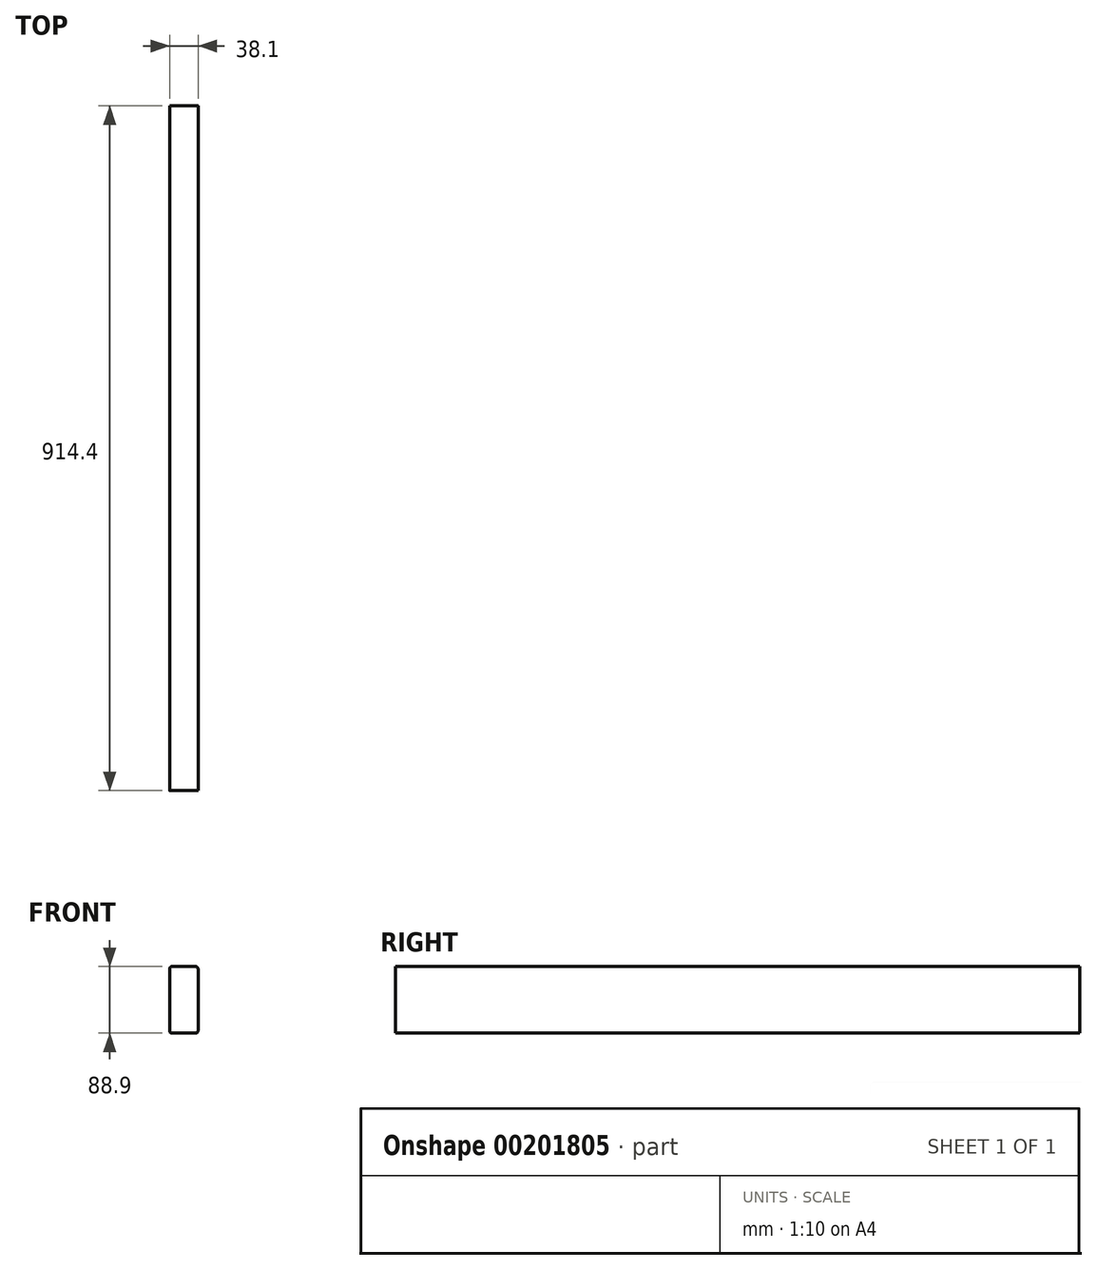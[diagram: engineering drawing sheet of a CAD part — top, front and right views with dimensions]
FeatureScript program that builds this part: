
annotation { "Feature Type Name" : "Feature", "Feature Type Description" : "" }
export const myFeature = defineFeature(function(context is Context, id is Id, definition is map)
    precondition{}
    {
        {
            var Q0;
            Q0=qCreatedBy(makeId("Front.planeOp"),FACE);
            var sketch = newSketch(context, id + "F0", { "sketchPlane" : qUnion([Q0])});
            skLineSegment(sketch, "E0.bottom", {"start": v(15.88, -44.45) * mm, "end": v(-15.88, -44.45) * mm});
            skLineSegment(sketch, "E0.top", {"start": v(15.87, 44.45) * mm, "end": v(-15.88, 44.45) * mm});
            skLineSegment(sketch, "E0.left", {"start": v(19.05, -41.28) * mm, "end": v(19.05, 41.28) * mm});
            skLineSegment(sketch, "E0.right", {"start": v(-19.05, -41.28) * mm, "end": v(-19.05, 41.28) * mm});
            skPoint(sketch, "E0.middle", {"position": v(0, 0) * mm});
            skPoint(sketch, "E1.visualSharp", {"position": v(-19.05, 44.45) * mm});
            skArc(sketch, "E1.filletArc", {"start": v(-15.88, 44.45) * mm, "mid": v(-18.12, 43.52) * mm, "end": v(-19.05, 41.28) * mm});
            skPoint(sketch, "E2.visualSharp", {"position": v(19.05, 44.45) * mm});
            skArc(sketch, "E2.filletArc", {"start": v(19.05, 41.28) * mm, "mid": v(18.12, 43.52) * mm, "end": v(15.87, 44.45) * mm});
            skPoint(sketch, "E3.visualSharp", {"position": v(-19.05, -44.45) * mm});
            skArc(sketch, "E3.filletArc", {"start": v(-19.05, -41.28) * mm, "mid": v(-18.12, -43.52) * mm, "end": v(-15.88, -44.45) * mm});
            skPoint(sketch, "E4.visualSharp", {"position": v(19.05, -44.45) * mm});
            skArc(sketch, "E4.filletArc", {"start": v(15.88, -44.45) * mm, "mid": v(18.12, -43.52) * mm, "end": v(19.05, -41.28) * mm});
            skSolve(sketch);
        }
        {
            var Q0;
            Q0=qSketchRegion(id+"F0",true);
            extrude(context, id + "F1", {"entities" : qUnion([Q0]), "endBound" : BoundingType.SYMMETRIC, "depth" : 914.4 * mm});
        }
    });
